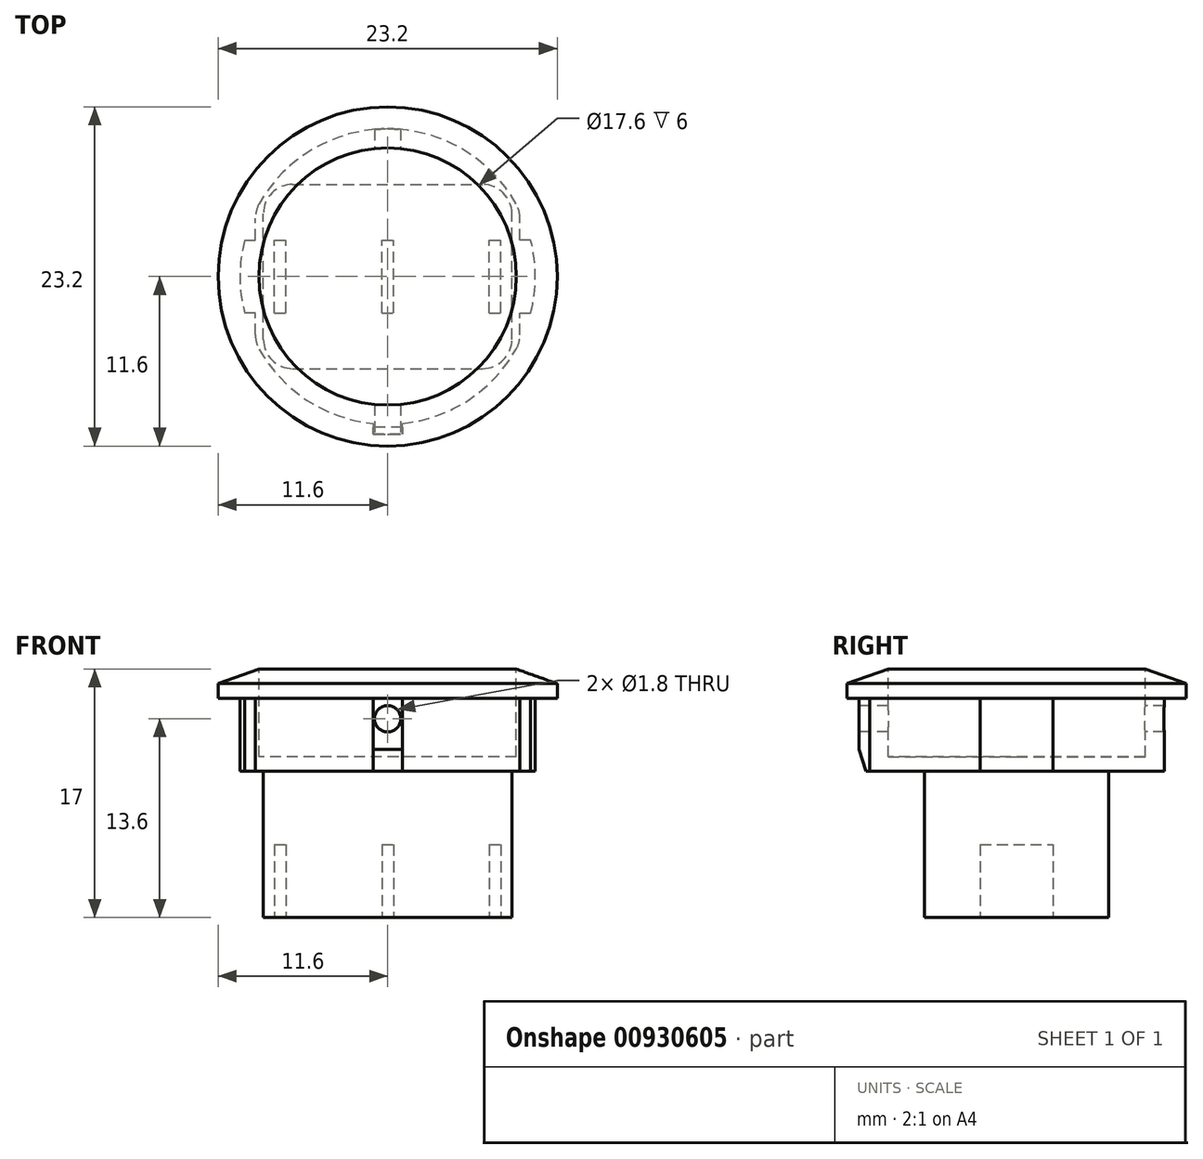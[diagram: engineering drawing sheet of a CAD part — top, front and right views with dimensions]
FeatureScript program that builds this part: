
annotation { "Feature Type Name" : "Feature", "Feature Type Description" : "" }
export const myFeature = defineFeature(function(context is Context, id is Id, definition is map)
    precondition{}
    {
        {
            var Q0;
            Q0=qCreatedBy(makeId("Top.planeOp"),FACE);
            var sketch = newSketch(context, id + "F0", { "sketchPlane" : qUnion([Q0])});
            skCircle(sketch, "E0", {"center": v(0, 0) * mm, "radius": 11.6 * mm});
            skSolve(sketch);
        }
        {
            var Q0;
            Q0=qSketchRegion(id+"F0",true);
            extrude(context, id + "F1", {"entities" : qUnion([Q0]), "depth" : 2 * mm, "offsetDistance" : 25 * mm});
        }
        {
            var Q0;
            Q0=makeQuery(id+"F1.opExtrude","CAP_FACE",FACE,{"disambiguationData":[OSD([sQuery(id+"F0.wireOp",EDGE,"E0")])],"isStart":true});
            var sketch = newSketch(context, id + "F2", { "sketchPlane" : qUnion([Q0])});
            skArc(sketch, "E1", {"start": v(-9.05, -4.48) * mm, "mid": v(0, -10.1) * mm, "end": v(9.05, -4.48) * mm});
            skLineSegment(sketch, "E2", {"start": v(-9.05, 4.48) * mm, "end": v(-9.05, -4.48) * mm});
            skLineSegment(sketch, "E3", {"start": v(9.05, 4.48) * mm, "end": v(9.05, -4.48) * mm});
            skArc(sketch, "E4.trimOffspring", {"start": v(9.05, 4.48) * mm, "mid": v(5.74, 8.3) * mm, "end": v(1, 10.05) * mm});
            skLineSegment(sketch, "E5", {"start": v(-1, 10.05) * mm, "end": v(-1, 10.8) * mm});
            skLineSegment(sketch, "E6", {"start": v(-1, 10.8) * mm, "end": v(1, 10.8) * mm});
            skLineSegment(sketch, "E7", {"start": v(1, 10.8) * mm, "end": v(1, 10.05) * mm});
            skArc(sketch, "E8.trimOffspring", {"start": v(-1, 10.05) * mm, "mid": v(-5.74, 8.3) * mm, "end": v(-9.05, 4.48) * mm});
            skLineSegment(sketch, "E9", {"start": v(-9.05, 2.5) * mm, "end": v(-9.79, 2.5) * mm});
            skLineSegment(sketch, "E10", {"start": v(-9.79, -2.5) * mm, "end": v(-9.05, -2.5) * mm});
            skLineSegment(sketch, "E11", {"start": v(9.05, 2.5) * mm, "end": v(9.79, 2.5) * mm});
            skLineSegment(sketch, "E12", {"start": v(9.79, -2.5) * mm, "end": v(9.05, -2.5) * mm});
            skArc(sketch, "E13", {"start": v(-9.05, 4.48) * mm, "mid": v(-9.47, 3.51) * mm, "end": v(-9.79, 2.5) * mm, "construction": true});
            skArc(sketch, "E14", {"start": v(9.05, -4.48) * mm, "mid": v(9.47, -3.51) * mm, "end": v(9.79, -2.5) * mm, "construction": true});
            skArc(sketch, "E15.trimOffspring", {"start": v(-9.79, -2.5) * mm, "mid": v(-9.47, -3.51) * mm, "end": v(-9.05, -4.48) * mm, "construction": true});
            skArc(sketch, "E16", {"start": v(-9.79, 2.5) * mm, "mid": v(-10.1, 0) * mm, "end": v(-9.79, -2.5) * mm});
            skArc(sketch, "E17.trimOffspring", {"start": v(9.79, 2.5) * mm, "mid": v(9.47, 3.51) * mm, "end": v(9.05, 4.48) * mm, "construction": true});
            skArc(sketch, "E18", {"start": v(9.79, -2.5) * mm, "mid": v(10.1, 0) * mm, "end": v(9.79, 2.5) * mm});
            skSolve(sketch);
        }
        {
            var Q0;
            Q0=qSketchRegion(id+"F2",true);
            extrude(context, id + "F3", {"entities" : qUnion([Q0]), "operationType" : NewBodyOperationType.ADD, "depth" : 5 * mm, "offsetDistance" : 25 * mm});
        }
        {
            var Q0;
            Q0=makeQuery(id+"F3.opExtrude","CAP_FACE",FACE,{"disambiguationData":[OSD([sQuery(id+"F2.wireOp",EDGE,"E1")])],"isStart":false});
            var sketch = newSketch(context, id + "F4", { "sketchPlane" : qUnion([Q0])});
            skLineSegment(sketch, "E19.bottom", {"start": v(-6.5, 6.3) * mm, "end": v(6.5, 6.3) * mm});
            skLineSegment(sketch, "E19.top", {"start": v(-6.5, -6.3) * mm, "end": v(6.5, -6.3) * mm});
            skLineSegment(sketch, "E19.left", {"start": v(-8.5, 4.3) * mm, "end": v(-8.5, -4.3) * mm});
            skLineSegment(sketch, "E19.right", {"start": v(8.5, 4.3) * mm, "end": v(8.5, -4.3) * mm});
            skPoint(sketch, "E20.visualSharp", {"position": v(-8.5, 6.3) * mm});
            skArc(sketch, "E20.filletArc", {"start": v(-6.5, 6.3) * mm, "mid": v(-7.91, 5.71) * mm, "end": v(-8.5, 4.3) * mm});
            skPoint(sketch, "E21.visualSharp", {"position": v(8.5, 6.3) * mm});
            skArc(sketch, "E21.filletArc", {"start": v(8.5, 4.3) * mm, "mid": v(7.91, 5.71) * mm, "end": v(6.5, 6.3) * mm});
            skPoint(sketch, "E22.visualSharp", {"position": v(8.5, -6.3) * mm});
            skArc(sketch, "E22.filletArc", {"start": v(6.5, -6.3) * mm, "mid": v(7.91, -5.71) * mm, "end": v(8.5, -4.3) * mm});
            skPoint(sketch, "E23.visualSharp", {"position": v(-8.5, -6.3) * mm});
            skArc(sketch, "E23.filletArc", {"start": v(-8.5, -4.3) * mm, "mid": v(-7.91, -5.71) * mm, "end": v(-6.5, -6.3) * mm});
            skSolve(sketch);
        }
        {
            var Q0;
            Q0=qSketchRegion(id+"F4",true);
            extrude(context, id + "F5", {"entities" : qUnion([Q0]), "operationType" : NewBodyOperationType.ADD, "depth" : 10 * mm, "offsetDistance" : 25 * mm});
        }
        {
            var Q0;
            Q0=makeQuery(id+"F5.opExtrude","CAP_FACE",FACE,{"disambiguationData":[OSD([sQuery(id+"F4.wireOp",EDGE,"E19.bottom"),sQuery(id+"F4.wireOp",EDGE,"E19.top"),sQuery(id+"F4.wireOp",EDGE,"E19.left"),sQuery(id+"F4.wireOp",EDGE,"E19.right"),sQuery(id+"F4.wireOp",EDGE,"E20.filletArc"),sQuery(id+"F4.wireOp",EDGE,"E21.filletArc"),sQuery(id+"F4.wireOp",EDGE,"E22.filletArc"),sQuery(id+"F4.wireOp",EDGE,"E23.filletArc")])],"isStart":false});
            var sketch = newSketch(context, id + "F6", { "sketchPlane" : qUnion([Q0])});
            skLineSegment(sketch, "E24.bottom", {"start": v(-0.4, 2.5) * mm, "end": v(0.4, 2.5) * mm});
            skLineSegment(sketch, "E24.top", {"start": v(-0.4, -2.5) * mm, "end": v(0.4, -2.5) * mm});
            skLineSegment(sketch, "E24.left", {"start": v(-0.4, 2.5) * mm, "end": v(-0.4, -2.5) * mm});
            skLineSegment(sketch, "E24.right", {"start": v(0.4, 2.5) * mm, "end": v(0.4, -2.5) * mm});
            skLineSegment(sketch, "E25.bottom", {"start": v(-7.75, 2.5) * mm, "end": v(-6.95, 2.5) * mm});
            skLineSegment(sketch, "E25.top", {"start": v(-7.75, -2.5) * mm, "end": v(-6.95, -2.5) * mm});
            skLineSegment(sketch, "E25.left", {"start": v(-7.75, 2.5) * mm, "end": v(-7.75, -2.5) * mm});
            skLineSegment(sketch, "E25.right", {"start": v(-6.95, 2.5) * mm, "end": v(-6.95, -2.5) * mm});
            skLineSegment(sketch, "E26.bottom", {"start": v(6.95, 2.5) * mm, "end": v(7.75, 2.5) * mm});
            skLineSegment(sketch, "E26.top", {"start": v(6.95, -2.5) * mm, "end": v(7.75, -2.5) * mm});
            skLineSegment(sketch, "E26.left", {"start": v(6.95, 2.5) * mm, "end": v(6.95, -2.5) * mm});
            skLineSegment(sketch, "E26.right", {"start": v(7.75, 2.5) * mm, "end": v(7.75, -2.5) * mm});
            skSolve(sketch);
        }
        {
            var Q0;
            Q0=qSketchRegion(id+"F6",true);
            extrude(context, id + "F7", {"entities" : qUnion([Q0]), "operationType" : NewBodyOperationType.REMOVE, "oppositeDirection" : true, "depth" : 5 * mm, "offsetDistance" : 25 * mm});
        }
        {
            var Q0;
            Q0=makeQuery(id+"F1.opExtrude","CAP_FACE",FACE,{"disambiguationData":[OSD([sQuery(id+"F0.wireOp",EDGE,"E0")])],"isStart":false});
            var sketch = newSketch(context, id + "F8", { "sketchPlane" : qUnion([Q0])});
            skCircle(sketch, "E27", {"center": v(0, 0) * mm, "radius": 8.8 * mm});
            skSolve(sketch);
        }
        {
            var Q0;
            Q0=qSketchRegion(id+"F8",true);
            extrude(context, id + "F9", {"entities" : qUnion([Q0]), "operationType" : NewBodyOperationType.REMOVE, "oppositeDirection" : true, "depth" : 6 * mm, "offsetDistance" : 25 * mm});
        }
        {
            var Q0;
            Q0=makeQuery(id+"F1.opExtrude","CAP_EDGE",EDGE,{"disambiguationData":[OSD([sQuery(id+"F0.wireOp",EDGE,"E0")])],"isStart":false});
            chamfer(context, id + "F10", {"entities" : qUnion([Q0]), "chamferType" : ChamferType.TWO_OFFSETS, "width1" : 2.8 * mm, "oppositeDirection" : false, "width2" : 1 * mm, "tangentPropagation" : true});
        }
        {
            var Q0;
            Q0=makeQuery(id+"F3.opExtrude","SWEPT_EDGE",EDGE,{"disambiguationData":[OSD([sQuery(id+"F2.wireOp",EDGE,"E1"),sQuery(id+"F2.wireOp",EDGE,"E2")])]});
            var Q1;
            Q1=makeQuery(id+"F3.opExtrude","SWEPT_EDGE",EDGE,{"disambiguationData":[OSD([sQuery(id+"F2.wireOp",EDGE,"E2"),sQuery(id+"F2.wireOp",EDGE,"E8.trimOffspring")])]});
            var Q2;
            Q2=makeQuery(id+"F3.opExtrude","SWEPT_EDGE",EDGE,{"disambiguationData":[OSD([sQuery(id+"F2.wireOp",EDGE,"E3"),sQuery(id+"F2.wireOp",EDGE,"E4.trimOffspring")])]});
            var Q3;
            Q3=makeQuery(id+"F3.opExtrude","SWEPT_EDGE",EDGE,{"disambiguationData":[OSD([sQuery(id+"F2.wireOp",EDGE,"E1"),sQuery(id+"F2.wireOp",EDGE,"E3")])]});
            fillet(context, id + "F11", {"entities" : qUnion([Q0, Q1, Q2, Q3]), "radius" : 2 * mm, "tangentPropagation" : true, "allowEdgeOverflow" : false});
        }
        {
            var Q0;
            Q0=makeQuery(id+"F3.opExtrude","CAP_EDGE",EDGE,{"disambiguationData":[OSD([sQuery(id+"F2.wireOp",EDGE,"E6")])],"isStart":false});
            chamfer(context, id + "F12", {"entities" : qUnion([Q0]), "chamferType" : ChamferType.TWO_OFFSETS, "width1" : 1.5 * mm, "oppositeDirection" : false, "width2" : 0.5 * mm, "tangentPropagation" : true});
        }
        {
            var Q0;
            Q0=makeQuery(id+"F3.opExtrude","SWEPT_FACE",FACE,{"disambiguationData":[OSD([sQuery(id+"F2.wireOp",EDGE,"E6")])]});
            var sketch = newSketch(context, id + "F13", { "sketchPlane" : qUnion([Q0])});
            skCircle(sketch, "E28", {"center": v(0, -1.4) * mm, "radius": 0.9 * mm});
            skSolve(sketch);
        }
        {
            var Q0;
            Q0=qSketchRegion(id+"F13",true);
            var Q1;
            Q1=makeQuery(id+"F3.opExtrude","SWEPT_FACE",FACE,{"disambiguationData":[OSD([sQuery(id+"F2.wireOp",EDGE,"E1")])]});
            extrude(context, id + "F14", {"entities" : qUnion([Q0]), "operationType" : NewBodyOperationType.REMOVE, "endBound" : BoundingType.THROUGH_ALL, "oppositeDirection" : true, "depth" : 25 * mm, "endBoundEntityFace" : qUnion([Q1]), "offsetDistance" : 25 * mm});
        }
    });
